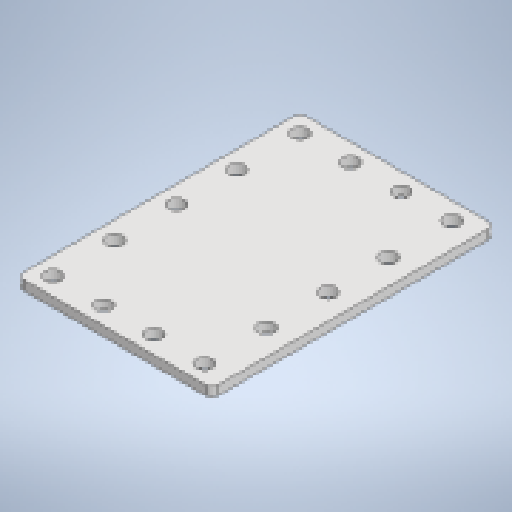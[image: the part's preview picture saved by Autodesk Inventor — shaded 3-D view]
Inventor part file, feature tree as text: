
AUTODESK INVENTOR PART (.ipt)
format: ipt  version: 2025.4 (Build 294407000, 407)  size: 243,200 bytes
history: native  units: mm
features: sketch x3, other x3, sheet_metal_op x1, chamfer x1, projected_geometry x1
ambient origin geometry x8: Origin, YZ Plane, XZ Plane, XY Plane, X Axis, Y Axis, Z Axis, Center Point
bodies: Body1 (feature_tree)
feature tree (9):
  sheet_metal_op  "Face2"
  chamfer  "Corner Round1"
  sketch  "Sketch2"  dims[d29=108.0mm]
  other  "Plate2"
  sketch  "Sketch5"  dims[d30=202.0mm d31=50.0mm d33=17.0mm d34=19.0mm d35=66.0mm d36=66.0mm d37=40.0mm d39=54.0mm d40=10.0mm d42=10.0mm d44=10.0mm d45=0.0mm d46=6.0mm]
  projected_geometry  "Projected Loop1"
  sketch  "Sketch Rectangular Pattern1"  dims[d14=10.0mm]
  other  "Cut3"
  other  "Definition1"
